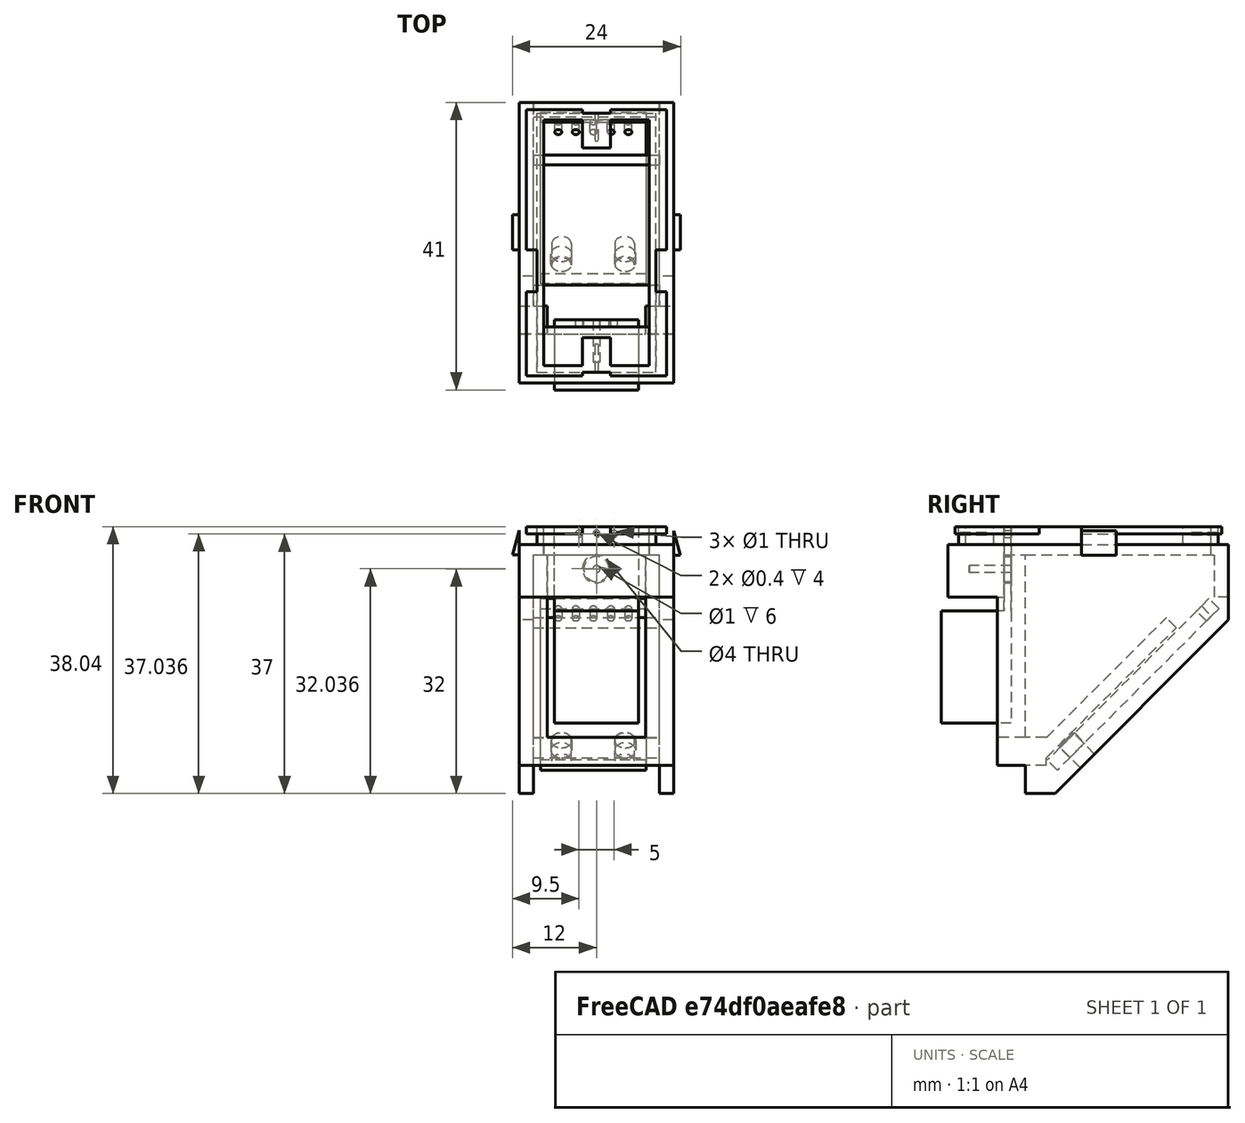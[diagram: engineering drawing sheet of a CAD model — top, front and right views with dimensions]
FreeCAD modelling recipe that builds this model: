
FCSTD DOCUMENT  (FreeCAD 0.17R13522 (Git))
Label: dht22AndBH1750
License: All rights reserved
LicenseURL: http://en.wikipedia.org/wiki/All_rights_reserved
objects: Part::Box×9, Part::Cylinder×4, Part::FeaturePython×3, Part::MultiFuse×3, Part::Cut×2
note: 21 computed .brp shape members not serialized (recipe doc carries the construction recipe); baked Part::Feature solids carry a one-line shape summary decoded from their .brp

FEATURE [Part::FeaturePython] BaseSensorMount_01  # a2plus imported part (geometry in sourceFile) (typed FeaturePython)
  fixedPosition = true
  sourceFile = <userpath>/PycharmProjects/PlantMonitor/Assembly/BaseParts/BaseSensorMount.FCStd
  timeLastImport = 1.52832e+09
  updateColors = true
FEATURE [Part::FeaturePython] Dht22Sensor_01  # a2plus imported part (geometry in sourceFile) (typed FeaturePython)
  Placement = pos=(11,9,-9) rot=(0,0.707107,-0.707107;3.14159rad)
  fixedPosition = false
  sourceFile = <userpath>/PycharmProjects/PlantMonitor/Assembly/ElectronicShapes/Dht22Sensor.FCStd
  timeLastImport = 1.52762e+09
  updateColors = true
FEATURE [Part::FeaturePython] BH1750FVI_01  # a2plus imported part (geometry in sourceFile) (typed FeaturePython)
  Placement = pos=(3,38.636,-7.62132) rot=(0.357407,0.357407,-0.862856;1.71777rad)
  fixedPosition = false
  sourceFile = <userpath>/PycharmProjects/PlantMonitor/Assembly/ElectronicShapes/BH1750FVI.FCStd
  timeLastImport = 1.52762e+09
  updateColors = true
FEATURE [Part::Box] Box  label="Cube"
  AttacherType = Attacher::AttachEngine3D
  Height = 7.5
  Length = 22
  Placement = pos=(0,0,-6) rot=(0,0,1;0rad)
  Width = 8
FEATURE [Part::Box] Box001  label="Cube001"
  AttacherType = Attacher::AttachEngine3D
  Height = 28
  Length = 4
  Placement = pos=(0,7,-28) rot=(0,0,1;0rad)
  Width = 4
FEATURE [Part::Box] Box002  label="Cube002"
  AttacherType = Attacher::AttachEngine3D
  Height = 28
  Length = 4
  Placement = pos=(18,7,-28) rot=(0,0,1;0rad)
  Width = 4
FEATURE [Part::Box] Box003  label="seitenwand1"
  AttacherType = Attacher::AttachEngine3D
  Height = 34
  Length = 2
  Placement = pos=(20,11,-34) rot=(0,0,1;0rad)
  Width = 29
FEATURE [Part::Box] Box004  label="seitenwand2"
  AttacherType = Attacher::AttachEngine3D
  Height = 34
  Length = 2
  Placement = pos=(0,11,-34) rot=(0,0,1;0rad)
  Width = 29
FEATURE [Part::Box] Box005  label="Cube005"
  AttacherType = Attacher::AttachEngine3D
  Height = 27
  Length = 22
  Placement = pos=(0,12.0353,-28.0355) rot=(-1,0,0;0.785398rad)
  Width = 2
FEATURE [Part::Box] Box006  label="Cube006"
  AttacherType = Attacher::AttachEngine3D
  Height = 4
  Length = 22
  Placement = pos=(0,7,-30) rot=(0,0,1;0rad)
  Width = 7
FEATURE [Part::Box] Box007  label="Cube007"
  AttacherType = Attacher::AttachEngine3D
  Height = 6
  Length = 22
  Placement = pos=(0,38,-6) rot=(0,0,1;0rad)
  Width = 2
FEATURE [Part::Cylinder] Cylinder001
  Angle = 360
  AttacherType = Attacher::AttachEngine3D
  Height = 4.5
  Placement = pos=(6,20,-29.5) rot=(1,0,0;0.785398rad)
  Radius = 1.4
FEATURE [Part::Cylinder] Cylinder002
  Angle = 360
  AttacherType = Attacher::AttachEngine3D
  Height = 4.5
  Placement = pos=(15,20,-29.5) rot=(1,0,0;0.785398rad)
  Radius = 1.4
FEATURE [Part::Box] Box008  label="cuttingcube"
  AttacherType = Attacher::AttachEngine3D
  Height = 38
  Length = 22
  Placement = pos=(0,13.9289,-35.3431) rot=(-1,0,0;0.785398rad)
  Width = 19
FEATURE [Part::Cylinder] Cylinder
  Angle = 360
  AttacherType = Attacher::AttachEngine3D
  Height = 4
  Placement = pos=(11,5,-2) rot=(-1,0,0;1.5708rad)
  Radius = 1.8
FEATURE [Part::MultiFuse] Fusion  label="Roughoutershape"
  Shapes = -> [Box,Box001,Box002,Box003,Cylinder,Box004]
FEATURE [Part::MultiFuse] Fusion001  label="guidedBHandDht"
  Shapes = -> [Fusion,Box005,Box007,Cylinder002,Box006,Cylinder001]
FEATURE [Part::Cut] Cut  label="SensorMount"
  Base = -> Fusion001
  Tool = -> Box008
FEATURE [Part::Cylinder] Cylinder003  label="screw_hole"
  Angle = 360
  AttacherType = Attacher::AttachEngine3D
  Height = 6
  Placement = pos=(11,9,-2) rot=(0,-0.707107,0.707107;3.14159rad)
  Radius = 0.5
FEATURE [Part::Cut] Cut001  label="upperMount"
  Base = -> Cut
  Tool = -> Cylinder003
FEATURE [Part::MultiFuse] Fusion002  label="DHT22_BH1750_SensorMount"
  Shapes = -> [Cut001,BaseSensorMount_01]
